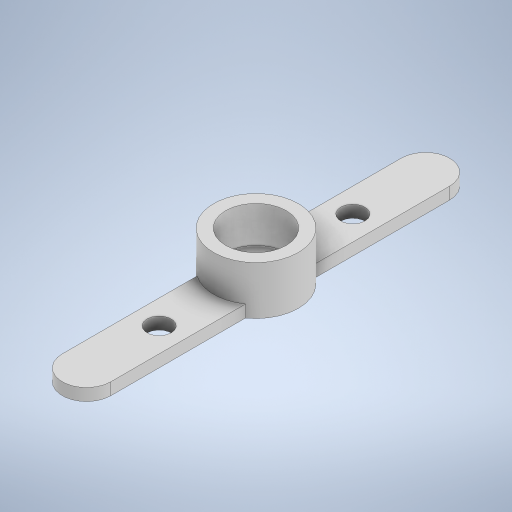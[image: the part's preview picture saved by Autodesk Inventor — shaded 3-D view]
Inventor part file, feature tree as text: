
AUTODESK INVENTOR PART (.ipt)
format: ipt  version: 2024.2 (Build 282272000, 272)  size: 303,616 bytes
history: native  units: mm
features: extrude x6, sketch x6, projected_geometry x3, fillet x1
ambient origin geometry x8: Origin, YZ Plane, XZ Plane, XY Plane, X Axis, Y Axis, Z Axis, Center Point
bodies: Solid1 (feature_tree)
feature tree (16):
  extrude  "Extrusion1"  Depth=1.0mm
  fillet  "Fillet1"  Radius=1.0mm
  extrude  "Extrusion2"  Depth=2.0mm
  extrude  "Extrusion3"  Depth=2.0mm
  extrude  "Extrusion4"  Depth=1.0mm TaperAngle=0.0deg
  extrude  "Extrusion5"  TaperAngle=0.0deg  [1 undecoded]
  extrude  "Extrusion6"  Depth=3.0mm TaperAngle=0.0deg
  sketch  "Sketch1"  dims[d0=4.0mm d1=32.0mm d2=1.0mm d3=0.0mm]
  sketch  "Sketch2"  dims[d4=2.0mm d5=7.0mm]
  sketch  "Sketch3"  dims[d6=16.0mm d7=2.0mm]
  projected_geometry  "Projected Loop1"
  projected_geometry  "Projected Loop2"
  sketch  "Sketch4"  dims[d8=3.0mm d9=0.0mm d10=1.0mm d11=0.0mm]
  projected_geometry  "Projected Loop3"
  sketch  "Sketch5"  dims[d12=2.0mm d13=0.0mm d14=0.0mm]
  sketch  "Sketch6"  dims[d15=5.0mm d16=3.0mm d17=0.0mm d18=2.0mm d19=2.0mm d20=16.0mm d21=8.0mm d22=0.0mm d23=0.0mm]
note: 1 required parameter value undecoded (feature->parameter linkage not recoverable at this tier; creation-order binding heuristic only, values carry confidence <= 0.55)
